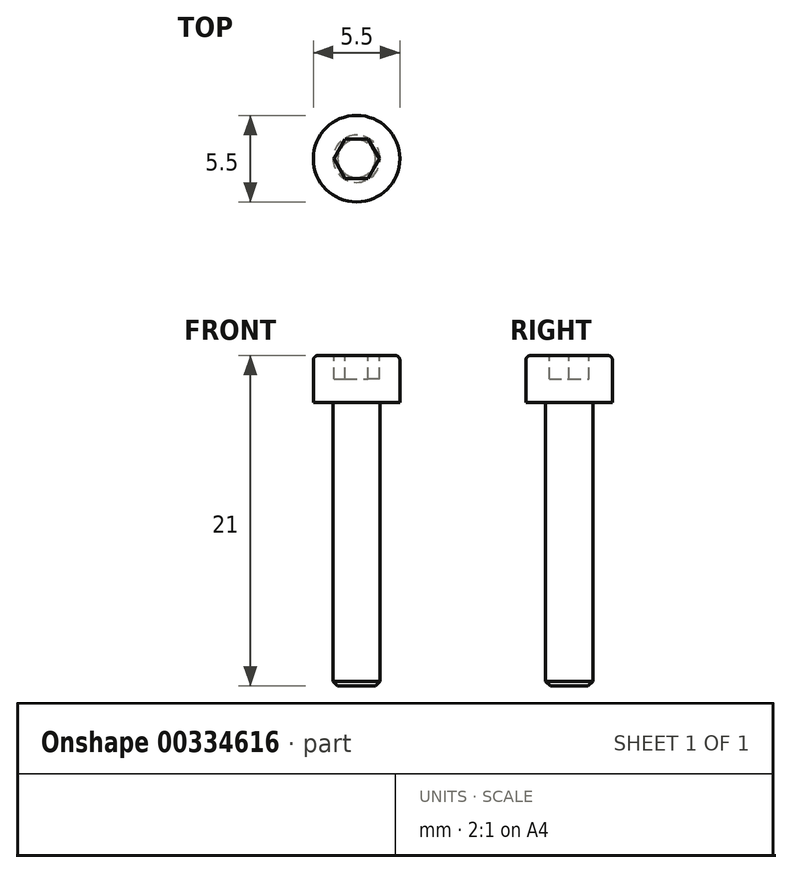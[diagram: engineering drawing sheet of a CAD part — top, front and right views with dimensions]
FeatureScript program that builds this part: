
annotation { "Feature Type Name" : "Feature", "Feature Type Description" : "" }
export const myFeature = defineFeature(function(context is Context, id is Id, definition is map)
    precondition{}
    {
        {
            var Q0;
            Q0=qCreatedBy(makeId("Top.planeOp"),FACE);
            var sketch = newSketch(context, id + "F0", { "sketchPlane" : qUnion([Q0])});
            skCircle(sketch, "E0", {"center": v(0, 0) * mm, "radius": 2.75 * mm});
            skSolve(sketch);
        }
        {
            var Q0;
            Q0=qSketchRegion(id+"F0",true);
            extrude(context, id + "F1", {"entities" : qUnion([Q0]), "depth" : 3 * mm});
        }
        {
            var Q0;
            Q0=makeQuery(id+"F1.opExtrude","CAP_FACE",FACE,{"disambiguationData":[OSD([sQuery(id+"F0.wireOp",EDGE,"E0")])],"isStart":true});
            var sketch = newSketch(context, id + "F2", { "sketchPlane" : qUnion([Q0])});
            skCircle(sketch, "E1", {"center": v(0, 0) * mm, "radius": 1.5 * mm});
            skSolve(sketch);
        }
        {
            var Q0;
            Q0=qSketchRegion(id+"F2",true);
            extrude(context, id + "F3", {"entities" : qUnion([Q0]), "operationType" : NewBodyOperationType.ADD, "depth" : 18 * mm});
        }
        {
            var Q0;
            Q0=makeQuery(id+"F3.opExtrude","CAP_EDGE",EDGE,{"disambiguationData":[OSD([sQuery(id+"F2.wireOp",EDGE,"E1")])],"isStart":false});
            chamfer(context, id + "F4", {"entities" : qUnion([Q0]), "width" : 0.3 * mm, "tangentPropagation" : true});
        }
        {
            var Q0;
            Q0=makeQuery(id+"F1.opExtrude","CAP_EDGE",EDGE,{"disambiguationData":[OSD([sQuery(id+"F0.wireOp",EDGE,"E0")])],"isStart":false});
            fillet(context, id + "F5", {"entities" : qUnion([Q0]), "radius" : 0.3 * mm, "tangentPropagation" : true, "allowEdgeOverflow" : false});
        }
        {
            var Q0;
            Q0=makeQuery(id+"F1.opExtrude","CAP_FACE",FACE,{"disambiguationData":[OSD([sQuery(id+"F0.wireOp",EDGE,"E0")])],"isStart":false});
            var sketch = newSketch(context, id + "F6", { "sketchPlane" : qUnion([Q0])});
            skCircle(sketch, "E2.cCircle", {"center": v(0, 0) * mm, "radius": 1.25 * mm, "construction": true});
            skLineSegment(sketch, "E2.0", {"start": v(-0.72, 1.25) * mm, "end": v(0.72, 1.25) * mm});
            skLineSegment(sketch, "E2.1", {"start": v(0.72, 1.25) * mm, "end": v(1.44, 0) * mm});
            skLineSegment(sketch, "E2.2", {"start": v(1.44, 0) * mm, "end": v(0.72, -1.25) * mm});
            skLineSegment(sketch, "E2.3", {"start": v(0.72, -1.25) * mm, "end": v(-0.72, -1.25) * mm});
            skLineSegment(sketch, "E2.4", {"start": v(-0.72, -1.25) * mm, "end": v(-1.44, 0) * mm});
            skLineSegment(sketch, "E2.5", {"start": v(-1.44, 0) * mm, "end": v(-0.72, 1.25) * mm});
            skPoint(sketch, "E2.0.midPoint", {"position": v(0, 1.25) * mm});
            skSolve(sketch);
        }
        {
            var Q0;
            Q0=qSketchRegion(id+"F6",true);
            extrude(context, id + "F7", {"entities" : qUnion([Q0]), "operationType" : NewBodyOperationType.REMOVE, "oppositeDirection" : true, "depth" : 1.5 * mm});
        }
    });
